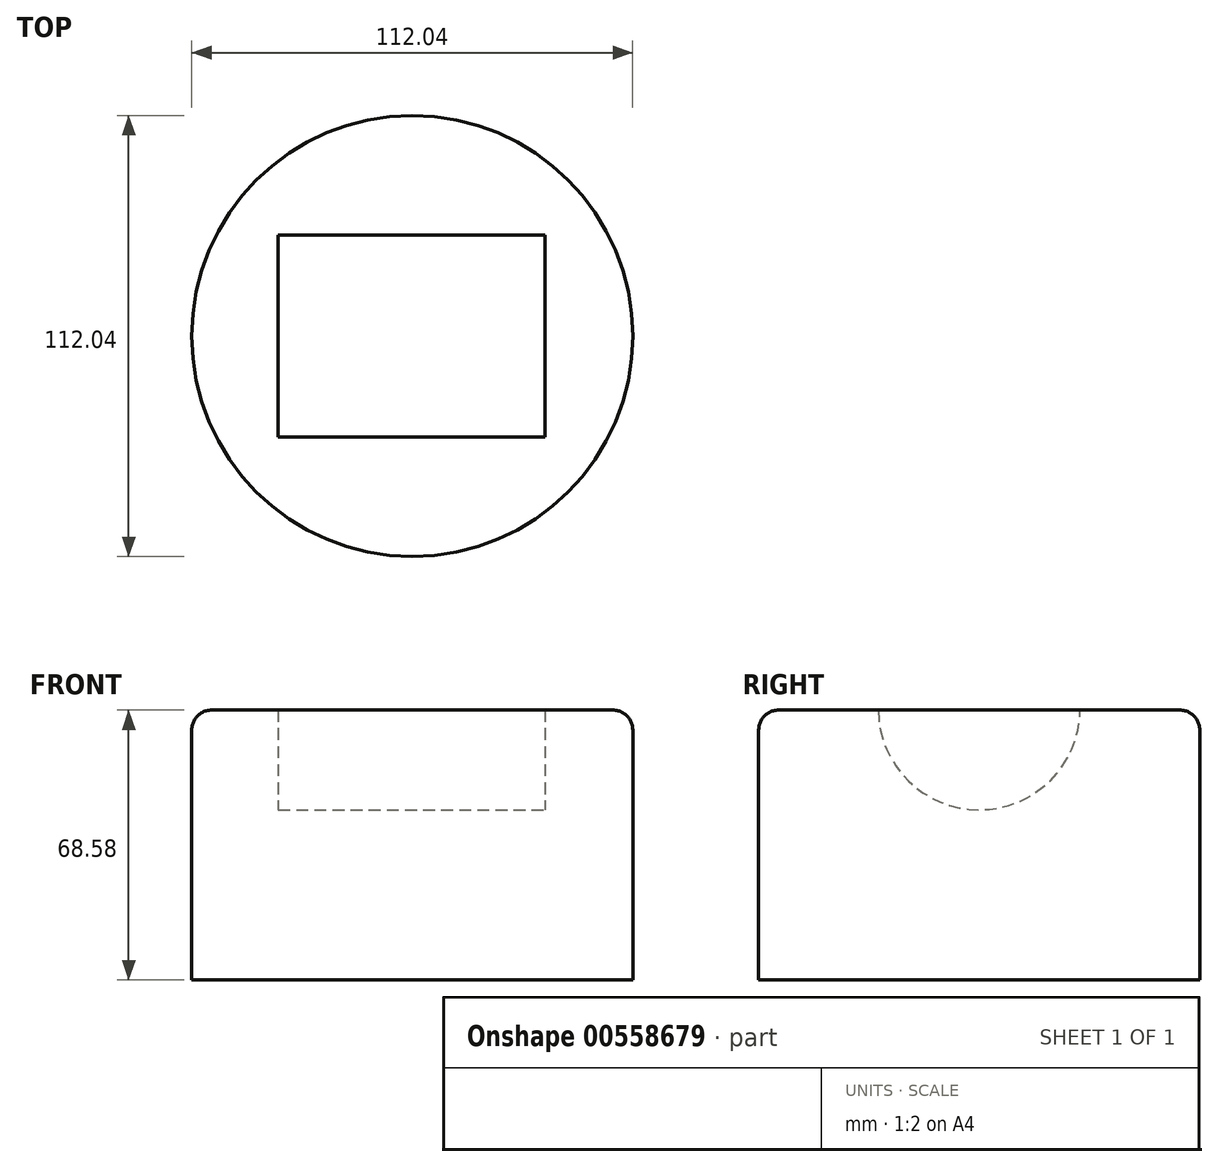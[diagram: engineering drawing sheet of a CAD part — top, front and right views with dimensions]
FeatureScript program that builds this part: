
annotation { "Feature Type Name" : "Feature", "Feature Type Description" : "" }
export const myFeature = defineFeature(function(context is Context, id is Id, definition is map)
    precondition{}
    {
        {
            var Q0;
            Q0=qCreatedBy(makeId("Top.planeOp"),FACE);
            var sketch = newSketch(context, id + "F0", { "sketchPlane" : qUnion([Q0])});
            skCircle(sketch, "E0", {"center": v(0, 0) * mm, "radius": 56.02 * mm});
            skSolve(sketch);
        }
        {
            var Q0;
            Q0=makeQuery(id+"F0.imprint","IMPRINT",FACE,{"disambiguationData":[TD([[makeQuery(id+"F0.imprint","IMPRINT",EDGE,{"derivedFrom":sQuery(id+"F0.wireOp",EDGE,"E0")}),1.0]])]});
            extrude(context, id + "F1", {"entities" : qUnion([Q0]), "depth" : 68.58 * mm, "offsetDistance" : 25.4 * mm});
        }
        {
            var Q0;
            Q0=qCreatedBy(makeId("Right.planeOp"),FACE);
            cPlane(context, id + "F2", {"entities" : qUnion([Q0]), "cplaneType" : CPlaneType.OFFSET, "offset" : 33.78 * mm, "width" : 152.4 * mm, "height" : 152.4 * mm});
        }
        {
            var Q0;
            Q0=qCreatedBy(id+"F2.planeOp",FACE);
            var sketch = newSketch(context, id + "F3", { "sketchPlane" : qUnion([Q0])});
            skLineSegment(sketch, "E1", {"start": v(0, 0) * mm, "end": v(0, 68.85) * mm});
            skCircle(sketch, "E2", {"center": v(0, 68.85) * mm, "radius": 25.64 * mm});
            skSolve(sketch);
        }
        {
            var Q0;
            Q0=makeQuery(id+"F3.imprint","IMPRINT",FACE,{"disambiguationData":[TD([[makeQuery(id+"F3.imprint","IMPRINT",EDGE,{"derivedFrom":sQuery(id+"F3.wireOp",EDGE,"E2")}),1.0]])]});
            var Q1;
            Q1=sQuery(id+"F3.wireOp",EDGE,"E2");
            extrude(context, id + "F4", {"entities" : qUnion([Q0]), "operationType" : NewBodyOperationType.REMOVE, "surfaceEntities" : qUnion([Q1]), "oppositeDirection" : true, "depth" : 67.82 * mm, "offsetDistance" : 25.4 * mm});
        }
        {
            var Q0;
            Q0=makeQuery(id+"F1.opExtrude","CAP_EDGE",EDGE,{"disambiguationData":[OSD([sQuery(id+"F0.wireOp",EDGE,"E0")])],"isStart":false});
            fillet(context, id + "F5", {"entities" : qUnion([Q0]), "radius" : 5.08 * mm, "tangentPropagation" : true, "allowEdgeOverflow" : false});
        }
    });
